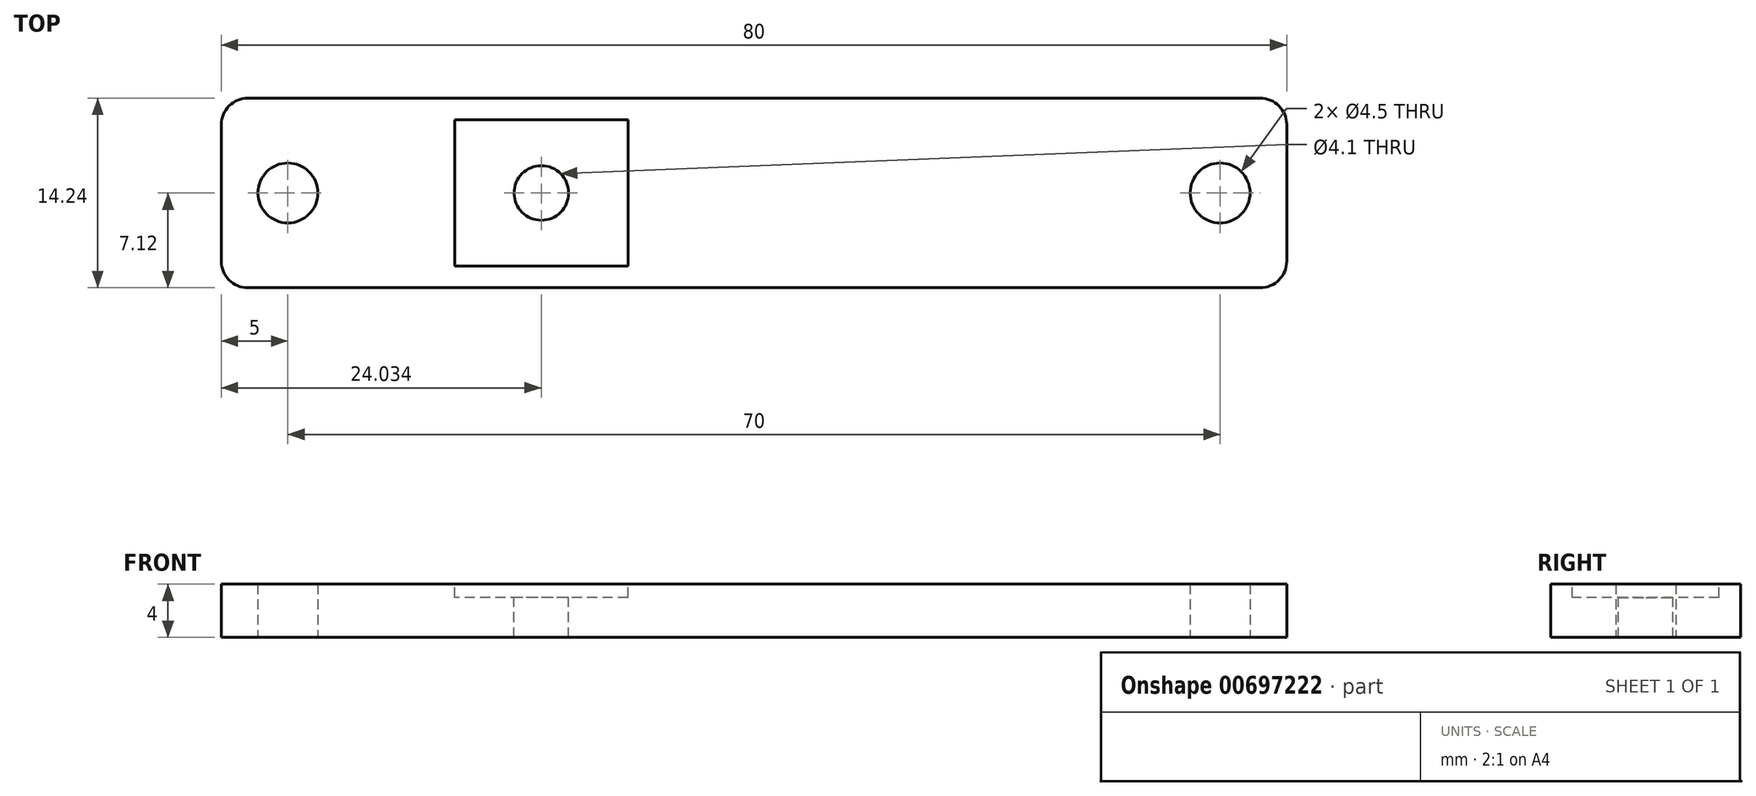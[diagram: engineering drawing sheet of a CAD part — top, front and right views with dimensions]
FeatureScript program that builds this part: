
annotation { "Feature Type Name" : "Feature", "Feature Type Description" : "" }
export const myFeature = defineFeature(function(context is Context, id is Id, definition is map)
    precondition{}
    {
        {
            var Q0;
            Q0=qCreatedBy(makeId("Top.planeOp"),FACE);
            var sketch = newSketch(context, id + "F0", { "sketchPlane" : qUnion([Q0])});
            skLineSegment(sketch, "E0.bottom", {"start": v(38, 7.12) * mm, "end": v(-38, 7.12) * mm});
            skLineSegment(sketch, "E0.top", {"start": v(38, -7.12) * mm, "end": v(-38, -7.12) * mm});
            skLineSegment(sketch, "E0.left", {"start": v(40, 5.12) * mm, "end": v(40, -5.12) * mm});
            skLineSegment(sketch, "E0.right", {"start": v(-40, 5.12) * mm, "end": v(-40, -5.12) * mm});
            skPoint(sketch, "E0.middle", {"position": v(0, 0) * mm});
            skCircle(sketch, "E1", {"center": v(-35, 0) * mm, "radius": 2.25 * mm});
            skCircle(sketch, "E2", {"center": v(35, 0) * mm, "radius": 2.25 * mm});
            skPoint(sketch, "E3.visualSharp", {"position": v(-40, 7.12) * mm});
            skArc(sketch, "E3.filletArc", {"start": v(-38, 7.12) * mm, "mid": v(-39.41, 6.53) * mm, "end": v(-40, 5.12) * mm});
            skPoint(sketch, "E4.visualSharp", {"position": v(-40, -7.12) * mm});
            skArc(sketch, "E4.filletArc", {"start": v(-40, -5.12) * mm, "mid": v(-39.41, -6.53) * mm, "end": v(-38, -7.12) * mm});
            skPoint(sketch, "E5.visualSharp", {"position": v(40, 7.12) * mm});
            skArc(sketch, "E5.filletArc", {"start": v(40, 5.12) * mm, "mid": v(39.41, 6.53) * mm, "end": v(38, 7.12) * mm});
            skPoint(sketch, "E6.visualSharp", {"position": v(40, -7.12) * mm});
            skArc(sketch, "E6.filletArc", {"start": v(38, -7.12) * mm, "mid": v(39.41, -6.53) * mm, "end": v(40, -5.12) * mm});
            skSolve(sketch);
        }
        {
            var Q0;
            Q0=makeQuery(id+"F0.imprint","IMPRINT",FACE,{"disambiguationData":[TD([[makeQuery(id+"F0.imprint","IMPRINT",EDGE,{"derivedFrom":sQuery(id+"F0.wireOp",EDGE,"E0.bottom")}),1.0]])]});
            extrude(context, id + "F1", {"entities" : qUnion([Q0]), "depth" : 4 * mm, "offsetDistance" : 25 * mm});
        }
        {
            var Q0;
            Q0=makeQuery(id+"F1.opExtrude","CAP_FACE",FACE,{"disambiguationData":[OSD([sQuery(id+"F0.wireOp",EDGE,"E0.bottom"),sQuery(id+"F0.wireOp",EDGE,"E0.top"),sQuery(id+"F0.wireOp",EDGE,"E0.left"),sQuery(id+"F0.wireOp",EDGE,"E0.right"),sQuery(id+"F0.wireOp",EDGE,"E1"),sQuery(id+"F0.wireOp",EDGE,"E2"),sQuery(id+"F0.wireOp",EDGE,"E3.filletArc"),sQuery(id+"F0.wireOp",EDGE,"E4.filletArc"),sQuery(id+"F0.wireOp",EDGE,"E5.filletArc"),sQuery(id+"F0.wireOp",EDGE,"E6.filletArc")])],"isStart":false});
            var sketch = newSketch(context, id + "F2", { "sketchPlane" : qUnion([Q0])});
            skCircle(sketch, "E7", {"center": v(-15.97, 0) * mm, "radius": 2.05 * mm});
            skSolve(sketch);
        }
        {
            var Q0;
            Q0=makeQuery(id+"F2.imprint","IMPRINT",FACE,{"disambiguationData":[TD([[makeQuery(id+"F2.imprint","IMPRINT",EDGE,{"derivedFrom":sQuery(id+"F2.wireOp",EDGE,"E7")}),1.0]])]});
            extrude(context, id + "F3", {"entities" : qUnion([Q0]), "operationType" : NewBodyOperationType.REMOVE, "oppositeDirection" : true, "depth" : 5 * mm, "offsetDistance" : 25 * mm});
        }
        {
            var Q0;
            Q0=makeQuery(id+"F1.opExtrude","CAP_FACE",FACE,{"disambiguationData":[OSD([sQuery(id+"F0.wireOp",EDGE,"E0.bottom"),sQuery(id+"F0.wireOp",EDGE,"E0.top"),sQuery(id+"F0.wireOp",EDGE,"E0.left"),sQuery(id+"F0.wireOp",EDGE,"E0.right"),sQuery(id+"F0.wireOp",EDGE,"E1"),sQuery(id+"F0.wireOp",EDGE,"E2"),sQuery(id+"F0.wireOp",EDGE,"E3.filletArc"),sQuery(id+"F0.wireOp",EDGE,"E4.filletArc"),sQuery(id+"F0.wireOp",EDGE,"E5.filletArc"),sQuery(id+"F0.wireOp",EDGE,"E6.filletArc")])],"isStart":false});
            var sketch = newSketch(context, id + "F4", { "sketchPlane" : qUnion([Q0])});
            skLineSegment(sketch, "E8.bottom", {"start": v(-9.47, 5.5) * mm, "end": v(-22.47, 5.5) * mm});
            skLineSegment(sketch, "E8.top", {"start": v(-9.47, -5.5) * mm, "end": v(-22.47, -5.5) * mm});
            skLineSegment(sketch, "E8.left", {"start": v(-9.47, 5.5) * mm, "end": v(-9.47, -5.5) * mm});
            skLineSegment(sketch, "E8.right", {"start": v(-22.47, 5.5) * mm, "end": v(-22.47, -5.5) * mm});
            skPoint(sketch, "E8.middle", {"position": v(-15.97, 0) * mm});
            skSolve(sketch);
        }
        {
            var Q0;
            Q0 = qSketchRegion(id + "F4", true);
            extrude(context, id + "F5", {"entities" : qUnion([Q0]), "operationType" : NewBodyOperationType.REMOVE, "oppositeDirection" : true, "depth" : 1 * mm, "offsetDistance" : 25 * mm});
        }
    });
